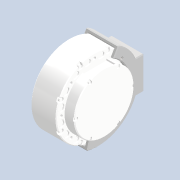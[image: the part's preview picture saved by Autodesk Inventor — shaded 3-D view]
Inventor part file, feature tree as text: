
AUTODESK INVENTOR PART (.ipt)
format: ipt  version: 2020.2 (Build 242310000, 310)  size: 1,575,936 bytes
history: native  units: in
note: dims shown in document units (in); Inventor stores cm internally (conversion verified against a paired STEP export)
features: other x15, extrude x1, sketch x1
ambient origin geometry x8: Origin, YZ Plane, XZ Plane, XY Plane, X Axis, Y Axis, Z Axis, Center Point
bodies: Solid1 (feature_tree)
feature tree (17):
  other  "Ensamble Final.iam"
  other  "Acople Aductor.ipt:1"
  other  "DIN 963 - M4 x 14.ipt:1"
  other  "DIN 963 - M4 x 14.ipt:2"
  other  "DIN 963 - M4 x 14.ipt:3"
  other  "DIN 916 - M4  x  8.ipt:1"
  other  "DIN 916 - M4  x  8.ipt:2"
  other  "DIN 916 - M4  x  8.ipt:3"
  other  "DIN 916 - M4  x  8.ipt:4"
  other  "DIN 916 - M4  x  8.ipt:5"
  other  "DIN 916 - M4  x  8.ipt:6"
  other  "DIN 916 - M4  x  8.ipt:7"
  other  "DIN 916 - M4  x  8.ipt:8"
  other  "Ensamble Pierna.Arnés13.iam:1::Ensamble Pierna.Arnés13.ipt:1"
  other  "Motor.ipt:2"
  extrude  "Extrusion1"  Depth=0.1969in
  sketch  "Sketch1"  dims[d0=0.3937in d1=0.1969in d2=0.0394in d3=0.0in]
